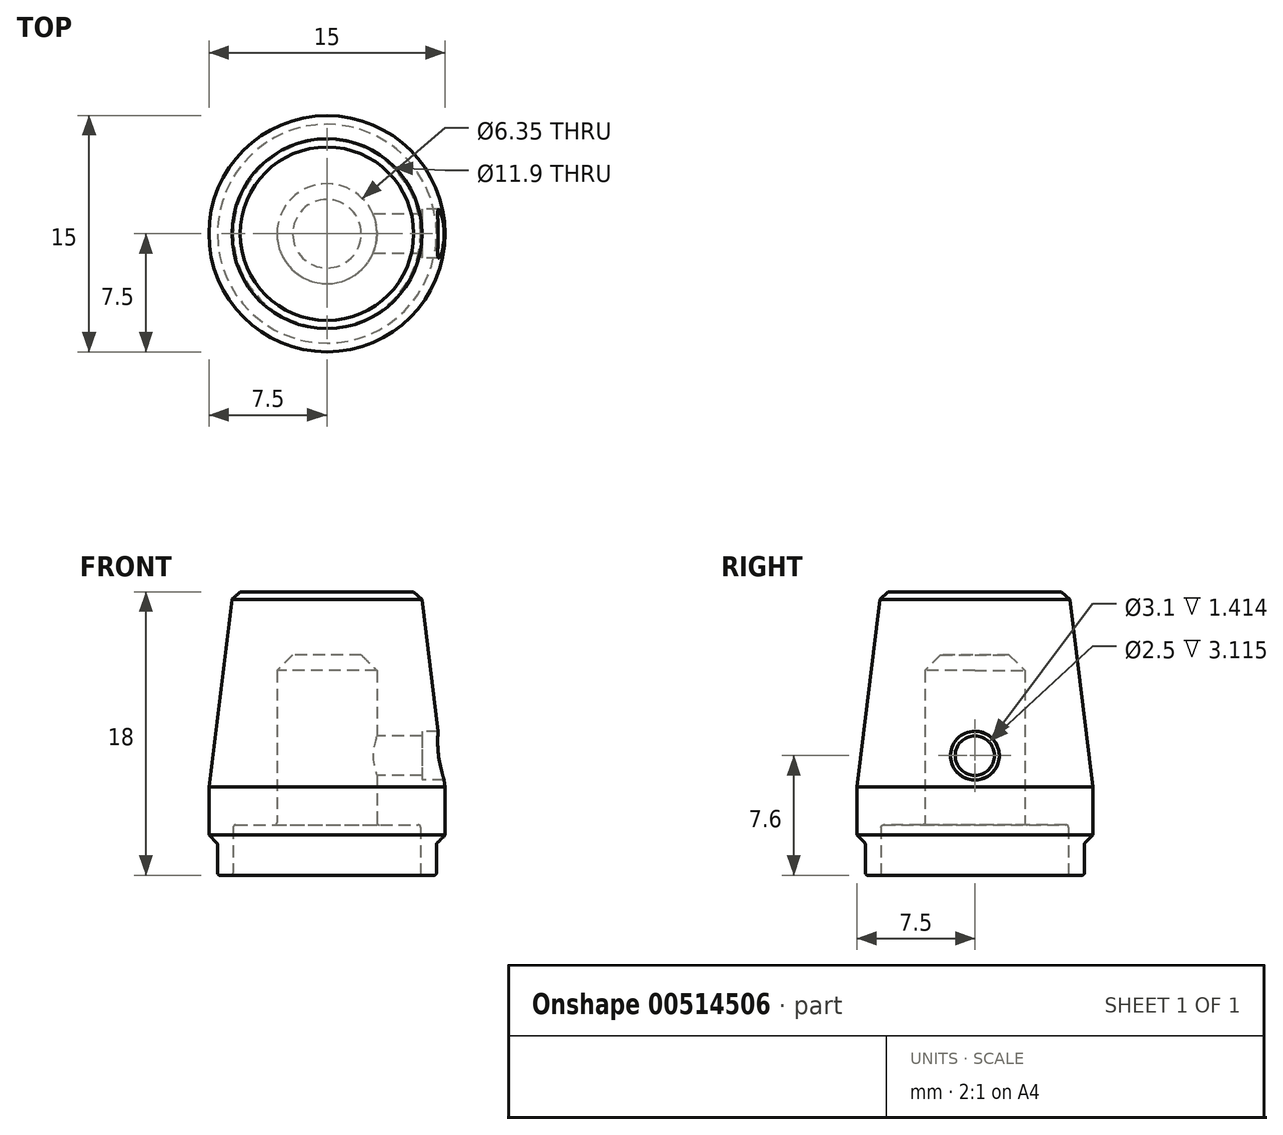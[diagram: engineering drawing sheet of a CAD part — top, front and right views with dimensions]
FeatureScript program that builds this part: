
annotation { "Feature Type Name" : "Feature", "Feature Type Description" : "" }
export const myFeature = defineFeature(function(context is Context, id is Id, definition is map)
    precondition{}
    {
        {
            var Q0;
            Q0=qCreatedBy(makeId("Front.planeOp"),FACE);
            var sketch = newSketch(context, id + "F0", { "sketchPlane" : qUnion([Q0])});
            skLineSegment(sketch, "E0.bottom", {"start": v(5.95, 0) * mm, "end": v(6.95, 0) * mm});
            skLineSegment(sketch, "E0.top", {"start": v(0, 18) * mm, "end": v(5.98, 18) * mm});
            skLineSegment(sketch, "E0.left", {"start": v(0, 3.2) * mm, "end": v(0, 18) * mm, "construction": true});
            skLineSegment(sketch, "E0.right", {"start": v(7.5, 2) * mm, "end": v(7.5, 5.6) * mm});
            skLineSegment(sketch, "E1", {"start": v(3.17, 3.2) * mm, "end": v(5.95, 3.2) * mm});
            skLineSegment(sketch, "E2", {"start": v(5.95, 3.2) * mm, "end": v(5.95, 0) * mm});
            skLineSegment(sketch, "E3", {"start": v(6.95, 0) * mm, "end": v(6.95, 2) * mm});
            skLineSegment(sketch, "E4", {"start": v(6.95, 2) * mm, "end": v(7.5, 2) * mm});
            skLineSegment(sketch, "E5", {"start": v(3.17, 3.2) * mm, "end": v(3.17, 14) * mm});
            skLineSegment(sketch, "E6", {"start": v(3.17, 14) * mm, "end": v(0, 14) * mm});
            skLineSegment(sketch, "E7", {"start": v(0, 18) * mm, "end": v(0, 14) * mm});
            skPoint(sketch, "E8", {"position": v(0, 7.6) * mm});
            skLineSegment(sketch, "E9", {"start": v(5.98, 18) * mm, "end": v(7.5, 5.6) * mm});
            skLineSegment(sketch, "E10", {"start": v(7.5, 5.6) * mm, "end": v(7.5, 20.36) * mm, "construction": true});
            skPoint(sketch, "E11", {"position": v(0, 0) * mm});
            skLineSegment(sketch, "E12", {"start": v(0, 7.6) * mm, "end": v(7.5, 7.6) * mm, "construction": true});
            skPoint(sketch, "E13", {"position": v(7.5, 7.6) * mm});
            skSolve(sketch);
        }
        {
            var Q0;
            Q0=qSketchRegion(id+"F0",true);
            var Q1;
            Q1=sQuery(id+"F0.wireOp",EDGE,"E0.left");
            revolve(context, id + "F1", {"entities" : qUnion([Q0]), "axis" : qUnion([Q1]), "revolveType" : RevolveType.FULL});
        }
        {
            var Q0;
            Q0=makeQuery(id+"F1.opRevolve","SWEPT_EDGE",EDGE,{"disambiguationData":[OSD([sQuery(id+"F0.wireOp",EDGE,"E0.right"),sQuery(id+"F0.wireOp",EDGE,"E4")])]});
            chamfer(context, id + "F2", {"entities" : qUnion([Q0]), "width" : .55 * mm});
        }
        {
            var Q0;
            Q0=makeQuery(id+"F1.opRevolve","SWEPT_EDGE",EDGE,{"disambiguationData":[OSD([sQuery(id+"F0.wireOp",EDGE,"E5"),sQuery(id+"F0.wireOp",EDGE,"E6")])]});
            chamfer(context, id + "F3", {"entities" : qUnion([Q0]), "width" : 1 * mm, "tangentPropagation" : true});
        }
        {
            var Q0;
            Q0=makeQuery(id+"F1.opRevolve","SWEPT_EDGE",EDGE,{"disambiguationData":[OSD([sQuery(id+"F0.wireOp",EDGE,"E0.top"),sQuery(id+"F0.wireOp",EDGE,"E9")])]});
            chamfer(context, id + "F4", {"entities" : qUnion([Q0]), "width" : .47 * mm, "tangentPropagation" : true});
        }
        {
            var Q0;
            Q0=makeQuery(id+"F1.opRevolve","SWEPT_FACE",FACE,{"disambiguationData":[OSD([sQuery(id+"F0.wireOp",EDGE,"E0.bottom")])]});
            var Q1;
            Q1=makeQuery(id+"F1.opRevolve","SWEPT_EDGE",EDGE,{"disambiguationData":[OSD([sQuery(id+"F0.wireOp",EDGE,"E1"),sQuery(id+"F0.wireOp",EDGE,"E2")])]});
            var Q2;
            Q2=makeQuery(id+"F1.opRevolve","SWEPT_EDGE",EDGE,{"disambiguationData":[OSD([sQuery(id+"F0.wireOp",EDGE,"E1"),sQuery(id+"F0.wireOp",EDGE,"E5")])]});
            var Q3;
            Q3=makeQuery(id+"F2.opChamfer","BLEND_EDGE",EDGE,{"blendedFrom":[makeQuery(id+"F1.opRevolve","SWEPT_EDGE",EDGE,{"disambiguationData":[OSD([sQuery(id+"F0.wireOp",EDGE,"E0.right"),sQuery(id+"F0.wireOp",EDGE,"E4")])]}),makeQuery(id+"F1.opRevolve","SWEPT_FACE",FACE,{"disambiguationData":[OSD([sQuery(id+"F0.wireOp",EDGE,"E3")])]})],"blendedInto":[makeQuery(id+"F1.opRevolve","SWEPT_FACE",FACE,{"disambiguationData":[OSD([sQuery(id+"F0.wireOp",EDGE,"E3")])]})]});
            fillet(context, id + "F5", {"entities" : qUnion([Q0, Q1, Q2, Q3]), "radius" : 0.15 * mm, "tangentPropagation" : true, "allowEdgeOverflow" : false});
        }
        {
            var Q0;
            Q0=sQuery(id+"F0.wireOp",EDGE,"E0.right");
            cPlane(context, id + "F6", {"entities" : qUnion([Q0]), "cplaneType" : CPlaneType.LINE_ANGLE, "offset" : 25 * mm, "angle" : 0 * degree, "width" : 150 * mm, "height" : 150 * mm});
        }
        {
            var Q0;
            Q0=qCreatedBy(id+"F6.planeOp",FACE);
            var sketch = newSketch(context, id + "F7", { "sketchPlane" : qUnion([Q0])});
            skPoint(sketch, "E14.0", {"position": v(0, 7.6) * mm});
            skSolve(sketch);
        }
        {
            var Q0;
            Q0=sQuery(id+"F7.wireOp",VERTEX,"E14.0");
            var Q1;
            Q1=makeQuery(id+"F1.opRevolve","SWEPT_BODY",BODY,{"disambiguationData":[OSD([sQuery(id+"F0.wireOp",EDGE,"E0.bottom"),sQuery(id+"F0.wireOp",EDGE,"E0.top"),sQuery(id+"F0.wireOp",EDGE,"E0.right"),sQuery(id+"F0.wireOp",EDGE,"E1"),sQuery(id+"F0.wireOp",EDGE,"E2"),sQuery(id+"F0.wireOp",EDGE,"E3"),sQuery(id+"F0.wireOp",EDGE,"E4"),sQuery(id+"F0.wireOp",EDGE,"E5"),sQuery(id+"F0.wireOp",EDGE,"E6"),sQuery(id+"F0.wireOp",EDGE,"E7"),sQuery(id+"F0.wireOp",EDGE,"E9")])]});
            hole(context, id + "F8", {"style" : HoleStyle.C_BORE, "endStyle" : HoleEndStyle.BLIND, "holeDiameter" : 2.5 * mm, "cBoreDiameter" : 3.1 * mm, "cBoreDepth" : 1 * mm, "holeDepth" : 5 * mm, "isTappedThrough" : true, "tappedDepth" : 12 * mm, "tapClearance" : 3, "locations" : qUnion([Q0]), "scope" : qUnion([Q1]), "startStyle" : HoleStartStyle.PART});
        }
    });
